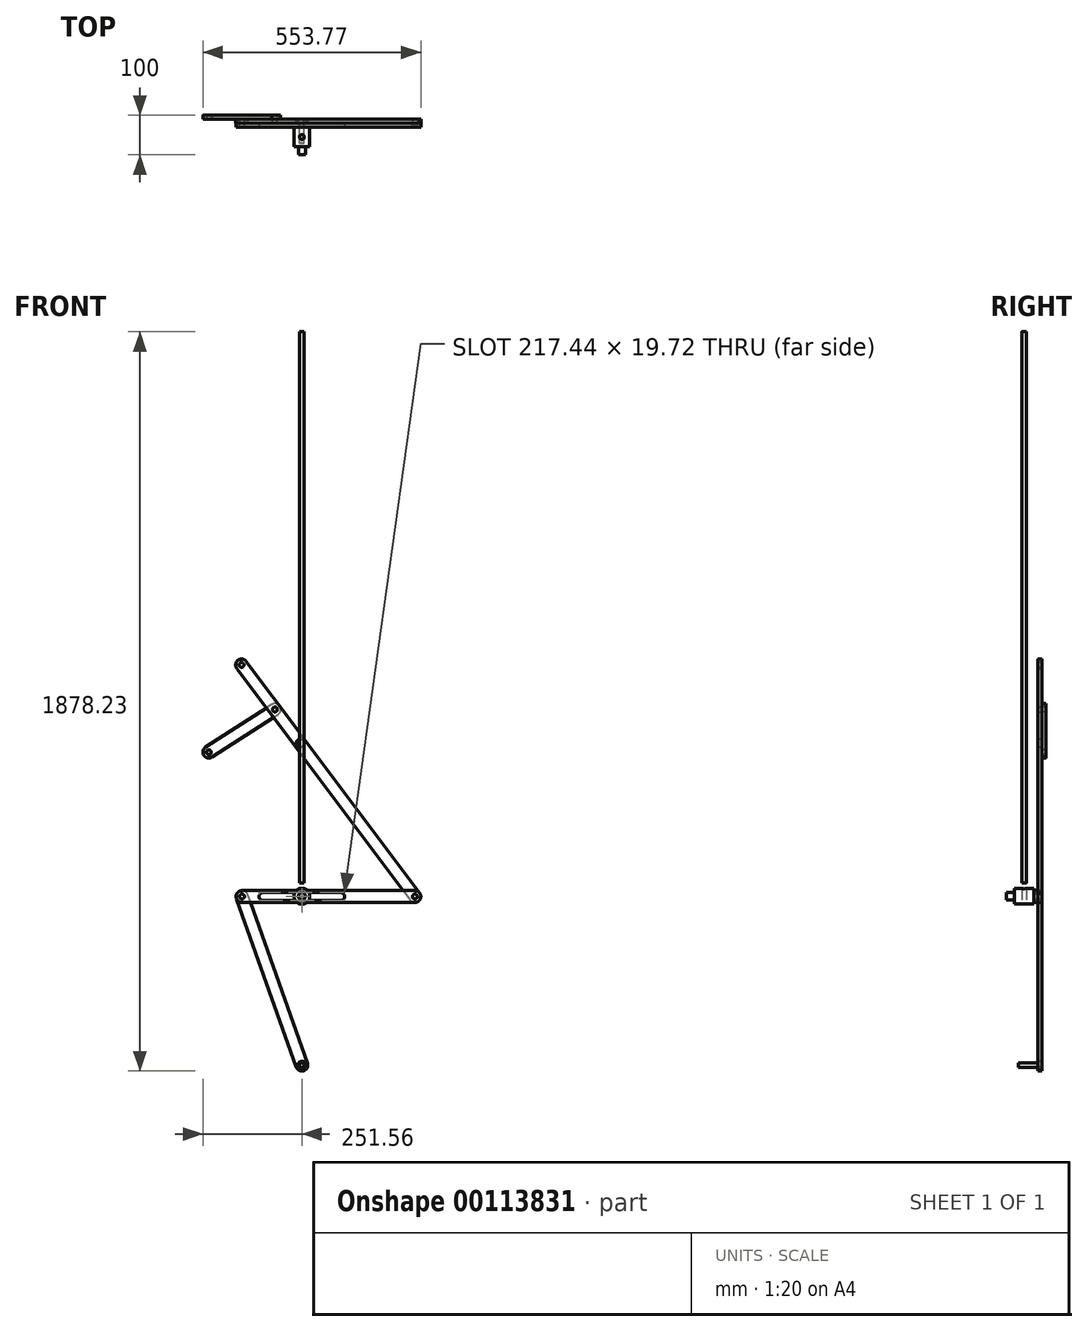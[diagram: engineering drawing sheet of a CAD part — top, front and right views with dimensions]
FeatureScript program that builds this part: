
annotation { "Feature Type Name" : "Feature", "Feature Type Description" : "" }
export const myFeature = defineFeature(function(context is Context, id is Id, definition is map)
    precondition{}
    {
        {
            var Q0;
            Q0=qCreatedBy(makeId("Top.planeOp"),FACE);
            var sketch = newSketch(context, id + "F0", { "sketchPlane" : qUnion([Q0])});
            skCircle(sketch, "E0", {"center": v(0, 0) * mm, "radius": 6 * mm});
            skSolve(sketch);
        }
        {
            var Q0;
            Q0 = qSketchRegion(id + "F0", true);
            extrude(context, id + "F1", {"entities" : qUnion([Q0]), "depth" : 1500 * mm});
        }
        {
            var Q0;
            Q0=qCreatedBy(makeId("Front.planeOp"),FACE);
            var sketch = newSketch(context, id + "F2", { "sketchPlane" : qUnion([Q0])});
            skCircle(sketch, "E1", {"center": v(0, 66.04) * mm, "radius": 20 * mm});
            skSolve(sketch);
        }
        {
            var Q0;
            Q0 = qSketchRegion(id + "F2", true);
            extrude(context, id + "F3", {"entities" : qUnion([Q0]), "depth" : 25 * mm, "hasSecondDirection" : true, "secondDirectionOppositeDirection" : true, "secondDirectionDepth" : 25 * mm});
        }
        {
            var Q0;
            Q0=makeQuery(id+"F3.opExtrude","CAP_FACE",FACE,{"disambiguationData":[OSD([sQuery(id+"F2.wireOp",EDGE,"E1")])],"isStart":false});
            var sketch = newSketch(context, id + "F4", { "sketchPlane" : qUnion([Q0])});
            skCircle(sketch, "E2", {"center": v(0, 66.04) * mm, "radius": 9 * mm});
            skSolve(sketch);
        }
        {
            var Q0;
            Q0 = qSketchRegion(id + "F4", true);
            extrude(context, id + "F5", {"entities" : qUnion([Q0]), "operationType" : NewBodyOperationType.ADD, "depth" : 20 * mm});
        }
        {
            var Q0;
            Q0=makeQuery(id+"F3.opExtrude","CAP_FACE",FACE,{"disambiguationData":[OSD([sQuery(id+"F2.wireOp",EDGE,"E1")])],"isStart":true});
            var sketch = newSketch(context, id + "F6", { "sketchPlane" : qUnion([Q0])});
            skCircle(sketch, "E3", {"center": v(0, 66.04) * mm, "radius": 9 * mm});
            skSolve(sketch);
        }
        {
            var Q0;
            Q0 = qSketchRegion(id + "F6", true);
            extrude(context, id + "F7", {"entities" : qUnion([Q0]), "operationType" : NewBodyOperationType.ADD, "depth" : 20 * mm});
        }
        {
            var Q0;
            Q0=qCreatedBy(makeId("Top.planeOp"),FACE);
            var sketch = newSketch(context, id + "F8", { "sketchPlane" : qUnion([Q0])});
            skCircle(sketch, "E4", {"center": v(0, 0) * mm, "radius": 6.1 * mm});
            skSolve(sketch);
        }
        {
            var Q0;
            Q0 = qSketchRegion(id + "F8", true);
            extrude(context, id + "F9", {"entities" : qUnion([Q0]), "operationType" : NewBodyOperationType.REMOVE, "depth" : 100 * mm});
        }
        {
            var Q0;
            Q0=makeQuery(id+"F3.opExtrude","CAP_FACE",FACE,{"disambiguationData":[OSD([sQuery(id+"F2.wireOp",EDGE,"E1")])],"isStart":true});
            var sketch = newSketch(context, id + "F10", { "sketchPlane" : qUnion([Q0])});
            skArc(sketch, "E5", {"start": v(-98.86, 75.04) * mm, "mid": v(-108.72, 65.18) * mm, "end": v(-98.86, 55.32) * mm});
            skLineSegment(sketch, "E6", {"start": v(98.86, 75.04) * mm, "end": v(-98.86, 75.04) * mm});
            skArc(sketch, "E7.MirrorC", {"start": v(98.86, 75.04) * mm, "mid": v(108.72, 65.18) * mm, "end": v(98.86, 55.32) * mm});
            skLineSegment(sketch, "E8", {"start": v(-98.86, 65.18) * mm, "end": v(152.06, 65.18) * mm, "construction": true});
            skLineSegment(sketch, "E9.MirrorCS", {"start": v(98.86, 55.32) * mm, "end": v(-98.86, 55.32) * mm});
            skLineSegment(sketch, "E10", {"start": v(-98.86, 65.18) * mm, "end": v(-287.21, 65.18) * mm, "construction": true});
            skArc(sketch, "E11", {"start": v(-287.21, 80.18) * mm, "mid": v(-302.21, 64.87) * mm, "end": v(-286.6, 50.2) * mm});
            skArc(sketch, "E12", {"start": v(152.06, 50.18) * mm, "mid": v(167.06, 65.18) * mm, "end": v(152.06, 80.18) * mm});
            skLineSegment(sketch, "E13", {"start": v(-287.84, 50.2) * mm, "end": v(152.06, 50.18) * mm});
            skLineSegment(sketch, "E14", {"start": v(152.06, 50.18) * mm, "end": v(152.06, 80.18) * mm});
            skLineSegment(sketch, "E15", {"start": v(152.06, 80.18) * mm, "end": v(-287.21, 80.18) * mm});
            skSolve(sketch);
        }
        {
            var Q0;
            Q0 = qSketchRegion(id + "F10", true);
            extrude(context, id + "F11", {"entities" : qUnion([Q0]), "depth" : 10 * mm});
        }
        {
            var Q0;
            Q0=makeQuery(id+"F11.opExtrude","CAP_FACE",FACE,{"disambiguationData":[OSD([sQuery(id+"F10.wireOp",EDGE,"E5"),sQuery(id+"F10.wireOp",EDGE,"E6"),sQuery(id+"F10.wireOp",EDGE,"E7.MirrorC"),sQuery(id+"F10.wireOp",EDGE,"E9.MirrorCS"),sQuery(id+"F10.wireOp",EDGE,"E11"),sQuery(id+"F10.wireOp",EDGE,"E12"),sQuery(id+"F10.wireOp",EDGE,"E13"),sQuery(id+"F10.wireOp",EDGE,"E15")])],"isStart":false});
            var sketch = newSketch(context, id + "F12", { "sketchPlane" : qUnion([Q0])});
            skCircle(sketch, "E16", {"center": v(-287.21, 65.18) * mm, "radius": 6.1 * mm});
            skSolve(sketch);
        }
        {
            var Q0;
            Q0 = qSketchRegion(id + "F12", true);
            extrude(context, id + "F13", {"entities" : qUnion([Q0]), "operationType" : NewBodyOperationType.REMOVE, "oppositeDirection" : true, "depth" : 25 * mm});
        }
        {
            var Q0;
            Q0=makeQuery(id+"F11.opExtrude","CAP_FACE",FACE,{"disambiguationData":[OSD([sQuery(id+"F10.wireOp",EDGE,"E5"),sQuery(id+"F10.wireOp",EDGE,"E6"),sQuery(id+"F10.wireOp",EDGE,"E7.MirrorC"),sQuery(id+"F10.wireOp",EDGE,"E9.MirrorCS"),sQuery(id+"F10.wireOp",EDGE,"E11"),sQuery(id+"F10.wireOp",EDGE,"E12"),sQuery(id+"F10.wireOp",EDGE,"E13"),sQuery(id+"F10.wireOp",EDGE,"E15")])],"isStart":false});
            var sketch = newSketch(context, id + "F14", { "sketchPlane" : qUnion([Q0])});
            skCircle(sketch, "E17", {"center": v(152.06, 65.18) * mm, "radius": 6.1 * mm});
            skSolve(sketch);
        }
        {
            var Q0;
            Q0 = qSketchRegion(id + "F14", true);
            extrude(context, id + "F15", {"entities" : qUnion([Q0]), "operationType" : NewBodyOperationType.REMOVE, "oppositeDirection" : true, "depth" : 25 * mm});
        }
        {
            var Q0;
            Q0=makeQuery(id+"F11.opExtrude","CAP_FACE",FACE,{"disambiguationData":[OSD([sQuery(id+"F10.wireOp",EDGE,"E5"),sQuery(id+"F10.wireOp",EDGE,"E6"),sQuery(id+"F10.wireOp",EDGE,"E7.MirrorC"),sQuery(id+"F10.wireOp",EDGE,"E9.MirrorCS"),sQuery(id+"F10.wireOp",EDGE,"E11"),sQuery(id+"F10.wireOp",EDGE,"E12"),sQuery(id+"F10.wireOp",EDGE,"E13"),sQuery(id+"F10.wireOp",EDGE,"E15")])],"isStart":false});
            var sketch = newSketch(context, id + "F16", { "sketchPlane" : qUnion([Q0])});
            skLineSegment(sketch, "E18", {"start": v(-287.21, 65.18) * mm, "end": v(153.21, 653.64) * mm, "construction": true});
            skCircle(sketch, "E19", {"center": v(-287.21, 65.18) * mm, "radius": 5.53 * mm, "construction": true});
            skCircle(sketch, "E20", {"center": v(-287.21, 65.18) * mm, "radius": 6.1 * mm});
            skArc(sketch, "E21", {"start": v(-298.93, 74.55) * mm, "mid": v(-296.4, 53.32) * mm, "end": v(-275.2, 56.2) * mm});
            skCircle(sketch, "E22", {"center": v(153.21, 653.64) * mm, "radius": 6.1 * mm});
            skArc(sketch, "E23", {"start": v(164.27, 643.5) * mm, "mid": v(162.79, 665.19) * mm, "end": v(141.2, 662.63) * mm});
            skLineSegment(sketch, "E24", {"start": v(166.06, 645.9) * mm, "end": v(-275.2, 56.2) * mm});
            skLineSegment(sketch, "E25", {"start": v(-298.93, 74.55) * mm, "end": v(141.2, 662.63) * mm});
            skSolve(sketch);
        }
        {
            var Q0;
            Q0 = qSketchRegion(id + "F16", true);
            extrude(context, id + "F17", {"entities" : qUnion([Q0]), "depth" : 10 * mm});
        }
        {
            var Q0;
            Q0=makeQuery(id+"F11.opExtrude","CAP_FACE",FACE,{"disambiguationData":[OSD([sQuery(id+"F10.wireOp",EDGE,"E5"),sQuery(id+"F10.wireOp",EDGE,"E6"),sQuery(id+"F10.wireOp",EDGE,"E7.MirrorC"),sQuery(id+"F10.wireOp",EDGE,"E9.MirrorCS"),sQuery(id+"F10.wireOp",EDGE,"E11"),sQuery(id+"F10.wireOp",EDGE,"E12"),sQuery(id+"F10.wireOp",EDGE,"E13"),sQuery(id+"F10.wireOp",EDGE,"E15")])],"isStart":false});
            var sketch = newSketch(context, id + "F18", { "sketchPlane" : qUnion([Q0])});
            skCircle(sketch, "E26", {"center": v(152.06, 65.18) * mm, "radius": 6.1 * mm});
            skLineSegment(sketch, "E27", {"start": v(152.06, 65.18) * mm, "end": v(0, -363.23) * mm, "construction": true});
            skCircle(sketch, "E28", {"center": v(0, -363.23) * mm, "radius": 10 * mm});
            skArc(sketch, "E29", {"start": v(-14.14, -358.2) * mm, "mid": v(-4.94, -377.4) * mm, "end": v(14.2, -368.08) * mm});
            skArc(sketch, "E30", {"start": v(165.45, 58.41) * mm, "mid": v(157.63, 79.1) * mm, "end": v(137.7, 69.52) * mm});
            skLineSegment(sketch, "E31", {"start": v(138.18, 70.87) * mm, "end": v(-14.14, -358.2) * mm});
            skLineSegment(sketch, "E32", {"start": v(14.2, -368.08) * mm, "end": v(166.72, 62) * mm});
            skSolve(sketch);
        }
        {
            var Q0;
            Q0 = qSketchRegion(id + "F18", true);
            extrude(context, id + "F19", {"entities" : qUnion([Q0]), "depth" : 9.8 * mm});
        }
        {
            var Q0;
            Q0=makeQuery(id+"F17.opExtrude","CAP_FACE",FACE,{"disambiguationData":[OSD([sQuery(id+"F16.wireOp",EDGE,"E20"),sQuery(id+"F16.wireOp",EDGE,"E21"),sQuery(id+"F16.wireOp",EDGE,"E22"),sQuery(id+"F16.wireOp",EDGE,"E23"),sQuery(id+"F16.wireOp",EDGE,"E24"),sQuery(id+"F16.wireOp",EDGE,"E25")])],"isStart":false});
            var sketch = newSketch(context, id + "F20", { "sketchPlane" : qUnion([Q0])});
            skLineSegment(sketch, "E33", {"start": v(153.21, 653.64) * mm, "end": v(-287.21, 65.18) * mm, "construction": true});
            skCircle(sketch, "E34", {"center": v(4.47, 454.9) * mm, "radius": 10 * mm});
            skSolve(sketch);
        }
        {
            var Q0;
            Q0 = qSketchRegion(id + "F20", true);
            extrude(context, id + "F21", {"entities" : qUnion([Q0]), "operationType" : NewBodyOperationType.REMOVE, "oppositeDirection" : true, "depth" : 25 * mm});
        }
        {
            var Q0;
            Q0=makeQuery(id+"F17.opExtrude","CAP_FACE",FACE,{"disambiguationData":[OSD([sQuery(id+"F16.wireOp",EDGE,"E20"),sQuery(id+"F16.wireOp",EDGE,"E21"),sQuery(id+"F16.wireOp",EDGE,"E22"),sQuery(id+"F16.wireOp",EDGE,"E23"),sQuery(id+"F16.wireOp",EDGE,"E24"),sQuery(id+"F16.wireOp",EDGE,"E25")])],"isStart":false});
            var sketch = newSketch(context, id + "F22", { "sketchPlane" : qUnion([Q0])});
            skLineSegment(sketch, "E35", {"start": v(4.47, 454.9) * mm, "end": v(153.21, 653.64) * mm, "construction": true});
            skCircle(sketch, "E36", {"center": v(68.54, 540.5) * mm, "radius": 6.1 * mm});
            skSolve(sketch);
        }
        {
            var Q0;
            Q0 = qSketchRegion(id + "F22", true);
            extrude(context, id + "F23", {"entities" : qUnion([Q0]), "operationType" : NewBodyOperationType.REMOVE, "oppositeDirection" : true, "depth" : 25 * mm});
        }
        {
            var Q0;
            Q0=makeQuery(id+"F17.opExtrude","CAP_FACE",FACE,{"disambiguationData":[OSD([sQuery(id+"F16.wireOp",EDGE,"E20"),sQuery(id+"F16.wireOp",EDGE,"E21"),sQuery(id+"F16.wireOp",EDGE,"E22"),sQuery(id+"F16.wireOp",EDGE,"E23"),sQuery(id+"F16.wireOp",EDGE,"E24"),sQuery(id+"F16.wireOp",EDGE,"E25")])],"isStart":false});
            var sketch = newSketch(context, id + "F24", { "sketchPlane" : qUnion([Q0])});
            skCircle(sketch, "E37", {"center": v(68.54, 540.5) * mm, "radius": 15 * mm});
            skCircle(sketch, "E38", {"center": v(68.54, 540.5) * mm, "radius": 6.1 * mm});
            skLineSegment(sketch, "E39", {"start": v(68.54, 540.5) * mm, "end": v(236.56, 432.02) * mm});
            skCircle(sketch, "E40", {"center": v(236.56, 432.02) * mm, "radius": 6.1 * mm});
            skCircle(sketch, "E41", {"center": v(236.56, 432.02) * mm, "radius": 15 * mm});
            skLineSegment(sketch, "E42", {"start": v(77.35, 552.65) * mm, "end": v(244.7, 444.63) * mm});
            skLineSegment(sketch, "E43", {"start": v(228, 419.7) * mm, "end": v(60.4, 527.9) * mm});
            skSolve(sketch);
        }
        {
            var Q0;
            Q0 = qSketchRegion(id + "F24", true);
            extrude(context, id + "F25", {"entities" : qUnion([Q0]), "depth" : 10 * mm});
        }
        {
            var Q0;
            Q0=makeQuery(id+"F19.opExtrude","CAP_FACE",FACE,{"disambiguationData":[OSD([sQuery(id+"F18.wireOp",EDGE,"E26"),sQuery(id+"F18.wireOp",EDGE,"E28"),sQuery(id+"F18.wireOp",EDGE,"E29"),sQuery(id+"F18.wireOp",EDGE,"E30"),sQuery(id+"F18.wireOp",EDGE,"E31"),sQuery(id+"F18.wireOp",EDGE,"E32")])],"isStart":true});
            var sketch = newSketch(context, id + "F26", { "sketchPlane" : qUnion([Q0])});
            skCircle(sketch, "E44", {"center": v(0, -363.23) * mm, "radius": 6 * mm});
            skSolve(sketch);
        }
        {
            var Q0;
            Q0 = qSketchRegion(id + "F26", true);
            extrude(context, id + "F27", {"entities" : qUnion([Q0]), "depth" : 50 * mm});
        }
    });
